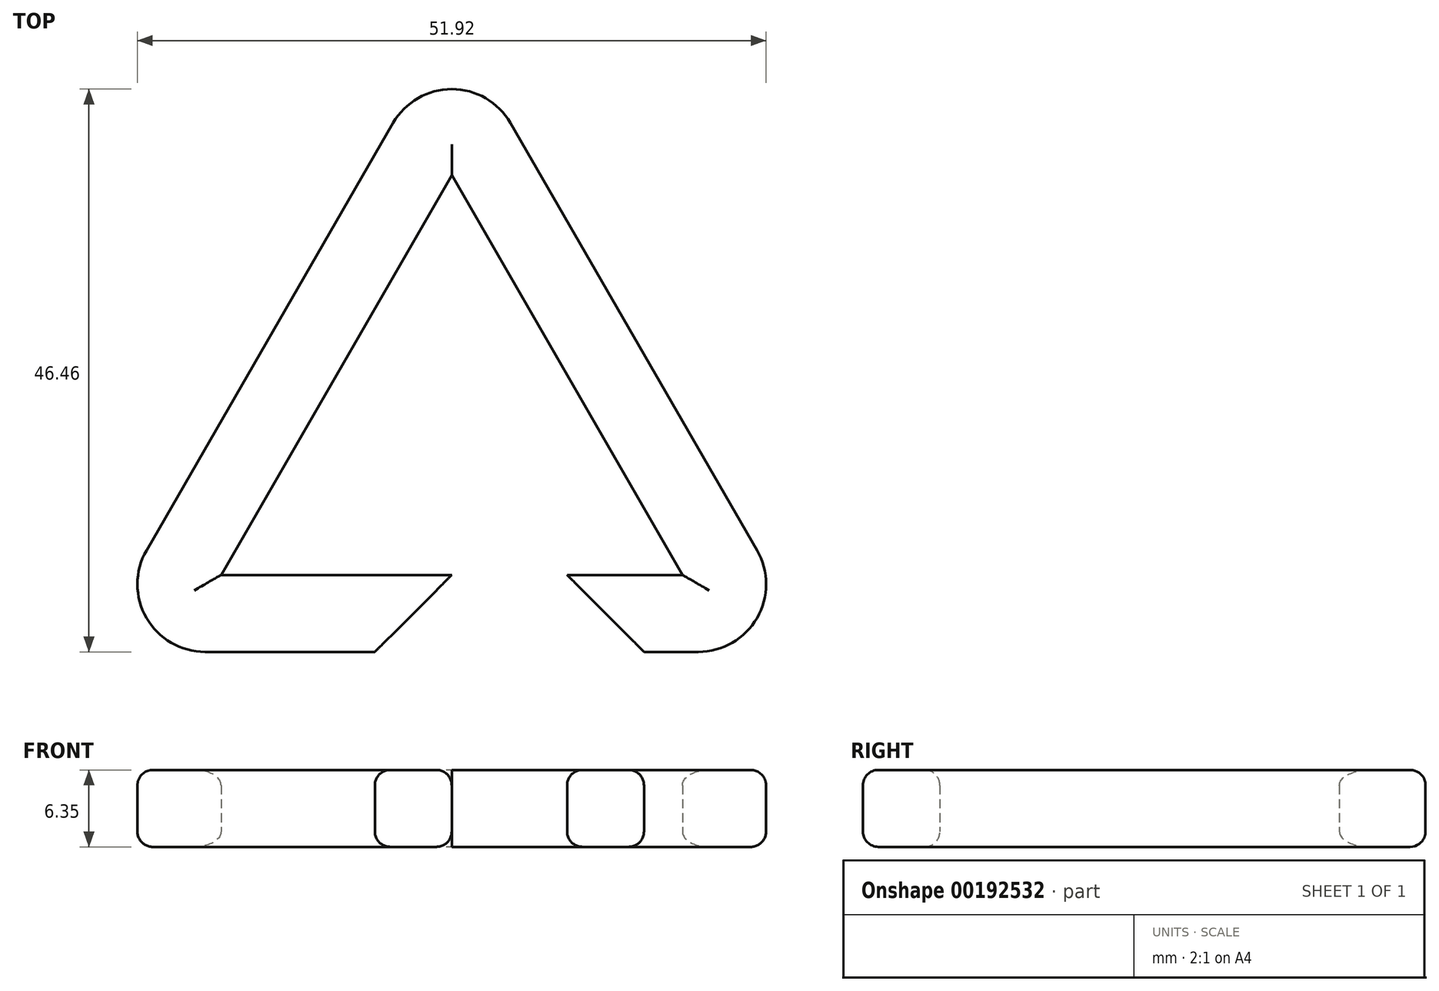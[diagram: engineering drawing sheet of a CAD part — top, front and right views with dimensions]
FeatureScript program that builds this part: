
annotation { "Feature Type Name" : "Feature", "Feature Type Description" : "" }
export const myFeature = defineFeature(function(context is Context, id is Id, definition is map)
    precondition{}
    {
        {
            var Q0;
            Q0=qCreatedBy(makeId("Top.planeOp"),FACE);
            var sketch = newSketch(context, id + "F0", { "sketchPlane" : qUnion([Q0])});
            skLineSegment(sketch, "E0", {"start": v(-30.05, -6.35) * mm, "end": v(0, 45.7) * mm});
            skLineSegment(sketch, "E1", {"start": v(0, 45.7) * mm, "end": v(30.05, -6.35) * mm});
            skLineSegment(sketch, "E2", {"start": v(30.05, -6.35) * mm, "end": v(15.87, -6.35) * mm});
            skLineSegment(sketch, "E3", {"start": v(15.87, -6.35) * mm, "end": v(9.52, 0) * mm});
            skLineSegment(sketch, "E4", {"start": v(9.52, 0) * mm, "end": v(19.05, 0) * mm});
            skLineSegment(sketch, "E5", {"start": v(19.05, 0) * mm, "end": v(0, 33) * mm});
            skLineSegment(sketch, "E6", {"start": v(0, 33) * mm, "end": v(-19.05, 0) * mm});
            skLineSegment(sketch, "E7", {"start": v(-19.05, 0) * mm, "end": v(0, 0) * mm});
            skLineSegment(sketch, "E8", {"start": v(0, 0) * mm, "end": v(-6.35, -6.35) * mm});
            skLineSegment(sketch, "E9", {"start": v(-6.35, -6.35) * mm, "end": v(-30.05, -6.35) * mm});
            skSolve(sketch);
        }
        {
            var Q0;
            Q0=makeQuery(id+"F0.imprint","IMPRINT",FACE,{"disambiguationData":[TD([[makeQuery(id+"F0.imprint","IMPRINT",EDGE,{"derivedFrom":sQuery(id+"F0.wireOp",EDGE,"E0")}),-1.0]])]});
            extrude(context, id + "F1", {"entities" : qUnion([Q0]), "depth" : 6.35 * mm});
        }
        {
            var Q0;
            Q0=makeQuery(id+"F1.opExtrude","SWEPT_EDGE",EDGE,{"disambiguationData":[OSD([sQuery(id+"F0.wireOp",EDGE,"E0"),sQuery(id+"F0.wireOp",EDGE,"E1")])]});
            var Q1;
            Q1=makeQuery(id+"F1.opExtrude","SWEPT_EDGE",EDGE,{"disambiguationData":[OSD([sQuery(id+"F0.wireOp",EDGE,"E0"),sQuery(id+"F0.wireOp",EDGE,"E9")])]});
            var Q2;
            Q2=makeQuery(id+"F1.opExtrude","SWEPT_EDGE",EDGE,{"disambiguationData":[OSD([sQuery(id+"F0.wireOp",EDGE,"E1"),sQuery(id+"F0.wireOp",EDGE,"E2")])]});
            fillet(context, id + "F2", {"entities" : qUnion([Q0, Q1, Q2]), "radius" : 5.6 * mm, "tangentPropagation" : true, "allowEdgeOverflow" : false});
        }
        {
            var Q0;
            Q0=makeQuery(id+"F1.opExtrude","CAP_EDGE",EDGE,{"disambiguationData":[OSD([sQuery(id+"F0.wireOp",EDGE,"E0")])],"isStart":false});
            var Q1;
            Q1=makeQuery(id+"F1.opExtrude","CAP_EDGE",EDGE,{"disambiguationData":[OSD([sQuery(id+"F0.wireOp",EDGE,"E0")])],"isStart":true});
            var Q2;
            Q2=makeQuery(id+"F1.opExtrude","CAP_EDGE",EDGE,{"disambiguationData":[OSD([sQuery(id+"F0.wireOp",EDGE,"E6")])],"isStart":true});
            var Q3;
            Q3=makeQuery(id+"F1.opExtrude","CAP_EDGE",EDGE,{"disambiguationData":[OSD([sQuery(id+"F0.wireOp",EDGE,"E5")])],"isStart":true});
            var Q4;
            Q4=makeQuery(id+"F1.opExtrude","CAP_EDGE",EDGE,{"disambiguationData":[OSD([sQuery(id+"F0.wireOp",EDGE,"E4")])],"isStart":true});
            var Q5;
            Q5=makeQuery(id+"F1.opExtrude","CAP_EDGE",EDGE,{"disambiguationData":[OSD([sQuery(id+"F0.wireOp",EDGE,"E7")])],"isStart":true});
            var Q6;
            Q6=makeQuery(id+"F1.opExtrude","CAP_EDGE",EDGE,{"disambiguationData":[OSD([sQuery(id+"F0.wireOp",EDGE,"E5")])],"isStart":false});
            var Q7;
            Q7=makeQuery(id+"F1.opExtrude","CAP_EDGE",EDGE,{"disambiguationData":[OSD([sQuery(id+"F0.wireOp",EDGE,"E6")])],"isStart":false});
            var Q8;
            Q8=makeQuery(id+"F1.opExtrude","CAP_EDGE",EDGE,{"disambiguationData":[OSD([sQuery(id+"F0.wireOp",EDGE,"E4")])],"isStart":false});
            var Q9;
            Q9=makeQuery(id+"F1.opExtrude","CAP_EDGE",EDGE,{"disambiguationData":[OSD([sQuery(id+"F0.wireOp",EDGE,"E7")])],"isStart":false});
            fillet(context, id + "F3", {"entities" : qUnion([Q0, Q1, Q2, Q3, Q4, Q5, Q6, Q7, Q8, Q9]), "radius" : 1.27 * mm, "tangentPropagation" : true, "allowEdgeOverflow" : false});
        }
    });
